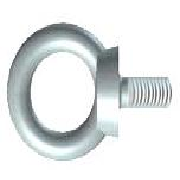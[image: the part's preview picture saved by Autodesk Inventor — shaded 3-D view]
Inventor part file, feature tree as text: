
AUTODESK INVENTOR PART (.ipt)
format: ipt  version: 2024 (Build 280153000, 153)  size: 256,512 bytes
history: native  units: mm (DEFAULTED — no unit token found)
features: extrude x2, other x1, thread x1
ambient origin geometry x8: Origin, YZ Plane, XZ Plane, XY Plane, X Axis, Y Axis, Z Axis, Center Point
bodies: Solid1 (feature_tree), Body (feature_tree)
feature tree (4):
  extrude  "Eye"  Depth=45.0mm
  extrude  "Cut"  Depth=90.0mm
  other  "Groove1"
  thread  "Thread2"  [1 undecoded]
note: 1 required parameter value undecoded (feature->parameter linkage not recoverable at this tier; creation-order binding heuristic only, values carry confidence <= 0.55)
